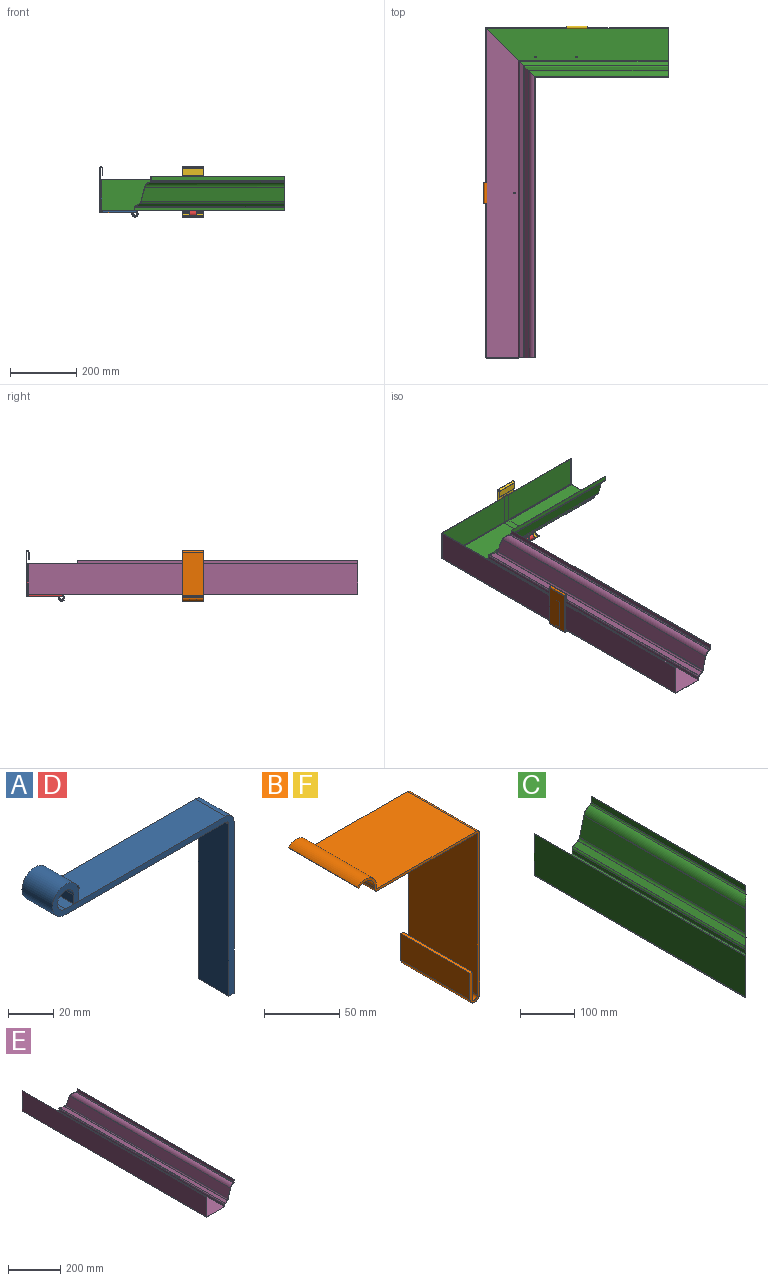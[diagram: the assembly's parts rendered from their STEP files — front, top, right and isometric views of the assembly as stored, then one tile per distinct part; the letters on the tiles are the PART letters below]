
ASSEMBLY  parts=6 mates=4
PART A: 15 faces, bbox 113.4x19x111.4 mm
  f0: plane 19x4.8mm, normal (-1,0,0), area 91.2mm2, adj f1,f11,f12,f13
  f1: plane 19x3.2mm, normal (0,0,-1), area 60.8mm2, adj f0,f2,f12,f13
  f2: plane 19x4.8mm, normal (1,0,0), area 91.2mm2, adj f1,f3,f12,f13
  f3: cylinder r=8.2mm len=19mm, axis (0,1,0), area 734.2mm2, adj f2,f4,f12,f13
  f4: plane 100x19mm, normal (0,0,-1), area 1880.4mm2, adj f3,f5,f12,f13,f14
  f5: cylinder r=2mm len=19mm, axis (0,1,0), area 59.7mm2, adj f4,f6,f12,f13
  f6: plane 92.98x19mm, normal (-1,0,0), area 1766.6mm2, adj f5,f7,f12,f13
  f7: plane 19x3.2mm, normal (0,0,-1), area 60.8mm2, adj f6,f8,f12,f13
  f8: plane 92.98x19mm, normal (1,0,0), area 1766.6mm2, adj f7,f9,f12,f13
  f9: cylinder r=5.2mm len=19mm, axis (0,1,0), area 155.2mm2, adj f8,f10,f12,f13
  f10: plane 100x19mm, normal (0,0,1), area 1880.4mm2, adj f9,f11,f12,f13,f14
  f11: cylinder r=5mm len=19mm, axis (0,1,0), area 447.7mm2, adj f0,f10,f12,f13
  f12: plane 113.4x111.38mm, normal (0,-1,0), area 750.5mm2, adj f0,f1,f2,f3,f4,f5,f6,f7
  f13: plane 113.4x111.38mm, normal (0,1,0), area 750.5mm2, adj f0,f1,f2,f3,f4,f5,f6,f7
  f14: cylinder r=2.5mm len=5mm, axis (0,0,-1), area 50.3mm2, adj f4,f10
PART B: 20 faces, bbox 114.9x65x152 mm
  f0: plane 65x1.7mm, normal (-1,0,0), area 110.5mm2, adj f1,f17,f18,f19
  f1: cylinder r=3mm len=65mm, axis (0,1,0), area 306.3mm2, adj f0,f2,f18,f19
  f2: plane 93x65mm, normal (0,0,-1), area 6045mm2, adj f1,f3,f18,f19
  f3: cylinder r=1mm len=65mm, axis (0,1,0), area 102.1mm2, adj f2,f4,f18,f19
  f4: plane 131.3x65mm, normal (-1,0,0), area 8534.5mm2, adj f3,f5,f18,f19
  f5: cylinder r=2.5mm len=65mm, axis (0,1,0), area 510.5mm2, adj f4,f6,f18,f19
  f6: plane 65x21.5mm, normal (1,0,0), area 1397.5mm2, adj f5,f7,f18,f19
  f7: plane 65x2mm, normal (0,0,1), area 130mm2, adj f6,f8,f18,f19
  f8: plane 65x21.5mm, normal (-1,0,0), area 1397.5mm2, adj f7,f9,f18,f19
  f9: cylinder r=4.5mm len=65mm, axis (0,1,0), area 918.9mm2, adj f8,f10,f18,f19
  f10: plane 131.3x65mm, normal (1,0,0), area 8534.5mm2, adj f9,f11,f18,f19
  f11: cylinder r=3mm len=65mm, axis (0,1,0), area 306.3mm2, adj f10,f12,f18,f19
  f12: plane 93x65mm, normal (0,0,1), area 6045mm2, adj f11,f13,f18,f19
  f13: cylinder r=1mm len=65mm, axis (0,1,0), area 102.1mm2, adj f12,f14,f18,f19
  f14: plane 65x1.7mm, normal (1,0,0), area 110.5mm2, adj f13,f15,f18,f19
  f15: cylinder r=10.5mm len=65mm, axis (0,1,0), area 1608.1mm2, adj f14,f16,f18,f19
  f16: plane 65x1.41mm, normal (-0.71,0,-0.71), area 130mm2, adj f15,f17,f18,f19
  f17: cylinder r=8.5mm len=65mm, axis (0,1,0), area 1301.8mm2, adj f0,f16,f18,f19
  f18: plane 152x114.92mm, normal (0,-1,0), area 574.3mm2, adj f0,f1,f2,f3,f4,f5,f6,f7
  f19: plane 152x114.92mm, normal (0,1,0), area 574.3mm2, adj f0,f1,f2,f3,f4,f5,f6,f7
PART C: 28 faces, bbox 150x552x105 mm
  f0: plane 550.05x98mm, normal (0,0,-1), area 49063.4mm2, adj f15,f16,f24,f25,f26,f27
  f1: plane 403.05x1mm, normal (0,0,1), area 402.5mm2, adj f2,f23,f24,f26
  f2: plane 403.05x13.63mm, normal (-1,0,0), area 5491.5mm2, adj f1,f3,f24,f26
  f3: cylinder r=4mm len=405.4mm, axis (0,1,0), area 1850.8mm2, adj f2,f4,f24,f26
  f4: cylinder r=21mm len=422.4mm, axis (0,1,0), area 10140.5mm2, adj f3,f5,f24,f26
  f5: plane 433.63x44.29mm, normal (-0.97,0,0.25), area 19557.9mm2, adj f4,f6,f24,f26
  f6: cylinder r=8.68mm len=437.63mm, axis (0,1,0), area 2983.2mm2, adj f5,f7,f24,f26
  f7: plane 450.1x12.46mm, normal (-0.51,0,0.86), area 6423.4mm2, adj f6,f8,f24,f26
  f8: cylinder r=6mm len=453.05mm, axis (0,1,0), area 2814.2mm2, adj f7,f9,f24,f26
  f9: plane 453.05x9mm, normal (-1,0,0), area 4077.4mm2, adj f8,f10,f24,f26
  f10: plane 550.05x97mm, normal (0,0,1), area 48610.8mm2, adj f9,f11,f24,f25,f26,f27
  f11: cylinder r=1mm len=551.05mm, axis (0,1,0), area 865mm2, adj f10,f12,f24,f26
  f12: plane 551.05x93mm, normal (1,0,0), area 51247.4mm2, adj f11,f13,f24,f26
  f13: plane 552.05x1mm, normal (0,0,1), area 551.5mm2, adj f12,f14,f24,f26
  f14: plane 552.05x93mm, normal (-1,0,0), area 51340.4mm2, adj f13,f15,f24,f26
  f15: cylinder r=2mm len=552.05mm, axis (0,1,0), area 1732mm2, adj f0,f14,f24,f26
  f16: plane 452.05x10mm, normal (1,0,0), area 4520.5mm2, adj f0,f17,f24,f26
  f17: cylinder r=5mm len=452.05mm, axis (0,1,0), area 2340.8mm2, adj f16,f18,f24,f26
  f18: plane 449.59x12.46mm, normal (0.51,0,-0.86), area 6416mm2, adj f17,f19,f24,f26
  f19: cylinder r=9.68mm len=437.13mm, axis (0,1,0), area 3320.9mm2, adj f18,f20,f24,f26
  f20: plane 432.66x44.29mm, normal (0.97,0,-0.25), area 19513.6mm2, adj f19,f21,f24,f26
  f21: cylinder r=20mm len=421.43mm, axis (0,1,0), area 9693.3mm2, adj f20,f22,f24,f26
  f22: cylinder r=5mm len=405.12mm, axis (0,1,0), area 2382.1mm2, adj f21,f23,f24,f26
  f23: plane 402.05x13.59mm, normal (1,0,0), area 5462.1mm2, adj f1,f22,f24,f26
  f24: plane 150x105mm, normal (0,1,0), area 318.2mm2, adj f0,f1,f2,f3,f4,f5,f6,f7
  f25: cylinder r=2.5mm len=5mm, axis (0,0,-1), area 15.7mm2, adj f0,f10
  f26: plane 150x150mm, normal (0.71,-0.71,0), area 450mm2, adj f0,f1,f2,f3,f4,f5,f6,f7
  f27: cylinder r=2.5mm len=5mm, axis (0,0,-1), area 15.7mm2, adj f0,f10
PART D: same geometry as A
PART E: 27 faces, bbox 150x998.5x105 mm
  f0: plane 849.46x1mm, normal (0,0,1), area 849mm2, adj f1,f23,f24,f25
  f1: plane 849.46x13.63mm, normal (-1,0,0), area 11573.9mm2, adj f0,f2,f24,f25
  f2: cylinder r=4mm len=851.81mm, axis (0,1,0), area 3896.6mm2, adj f1,f3,f24,f25
  f3: cylinder r=21mm len=868.81mm, axis (0,1,0), area 21036.8mm2, adj f2,f4,f24,f25
  f4: plane 880.04x44.29mm, normal (-0.97,0,0.25), area 39956.2mm2, adj f3,f5,f24,f25
  f5: cylinder r=8.68mm len=884.04mm, axis (0,1,0), area 6042.8mm2, adj f4,f6,f24,f25
  f6: plane 896.51x12.46mm, normal (-0.51,0,0.86), area 12883.6mm2, adj f5,f7,f24,f25
  f7: cylinder r=6mm len=899.46mm, axis (0,1,0), area 5593.4mm2, adj f6,f8,f24,f25
  f8: plane 899.46x9mm, normal (-1,0,0), area 8095.1mm2, adj f7,f9,f24,f25
  f9: plane 996.46x97mm, normal (0,0,1), area 91932.2mm2, adj f8,f10,f24,f25,f26
  f10: cylinder r=1mm len=997.46mm, axis (0,1,0), area 1566.2mm2, adj f9,f11,f24,f25
  f11: plane 997.46x93mm, normal (1,0,0), area 92763.5mm2, adj f10,f12,f24,f25
  f12: plane 998.46x1mm, normal (0,0,1), area 998mm2, adj f11,f13,f24,f25
  f13: plane 998.46x93mm, normal (-1,0,0), area 92856.5mm2, adj f12,f14,f24,f25
  f14: cylinder r=2mm len=998.46mm, axis (0,1,0), area 3134.5mm2, adj f13,f15,f24,f25
  f15: plane 996.46x98mm, normal (0,0,-1), area 92831.2mm2, adj f14,f16,f24,f25,f26
  f16: plane 898.46x10mm, normal (1,0,0), area 8984.6mm2, adj f15,f17,f24,f25
  f17: cylinder r=5mm len=898.46mm, axis (0,1,0), area 4656.8mm2, adj f16,f18,f24,f25
  f18: plane 896x12.46mm, normal (0.51,0,-0.86), area 12876.3mm2, adj f17,f19,f24,f25
  f19: cylinder r=9.68mm len=883.54mm, axis (0,1,0), area 6732.8mm2, adj f18,f20,f24,f25
  f20: plane 879.07x44.29mm, normal (0.97,0,-0.25), area 39911.9mm2, adj f19,f21,f24,f25
  f21: cylinder r=20mm len=867.84mm, axis (0,1,0), area 20126.4mm2, adj f20,f22,f24,f25
  f22: cylinder r=5mm len=851.53mm, axis (0,1,0), area 5020.1mm2, adj f21,f23,f24,f25
  f23: plane 848.46x13.59mm, normal (1,0,0), area 11527mm2, adj f0,f22,f24,f25
  f24: plane 150x105mm, normal (0,-1,0), area 318.2mm2, adj f0,f1,f2,f3,f4,f5,f6,f7
  f25: plane 150x150mm, normal (0.71,0.71,0), area 450mm2, adj f0,f1,f2,f3,f4,f5,f6,f7
  f26: cylinder r=2.5mm len=5mm, axis (0,0,-1), area 15.7mm2, adj f9,f15
PART F: same geometry as B
PLACE A rot(axis=(0,-1,0),180deg) t=(-940.87,-456.01,-110.16)mm
PLACE B rot(axis=(0,-1,0),180deg) t=(-956.5,-433.01,-102.46)mm
PLACE C rot(axis=(0,0,-1),90deg) t=(-458.08,-41.28,-49.48)mm
PLACE D rot(axis=(-0.71,-0.71,0),180deg) t=(-757.35,-68.28,-110.16)mm
PLACE E t=(-967.87,35.26,-49.48)mm
PLACE F rot(axis=(-0.71,-0.71,0),180deg) t=(-734.35,-52.65,-102.46)mm
MATE revolute D.f3 <-> F.f15  axis (1,0,0) through (-766.85,-68.28,-110.16)mm
MATE fastened E.f13 <-> A.f6  axis (-1,0,0) through (-1042.87,-465.51,-6.98)mm
MATE revolute A.f3 <-> B.f15  axis (0,1,0) through (-940.87,-465.51,-110.16)mm
MATE fastened D.f6 <-> C.f14  axis (0,-1,0) through (-766.85,33.72,-6.98)mm
